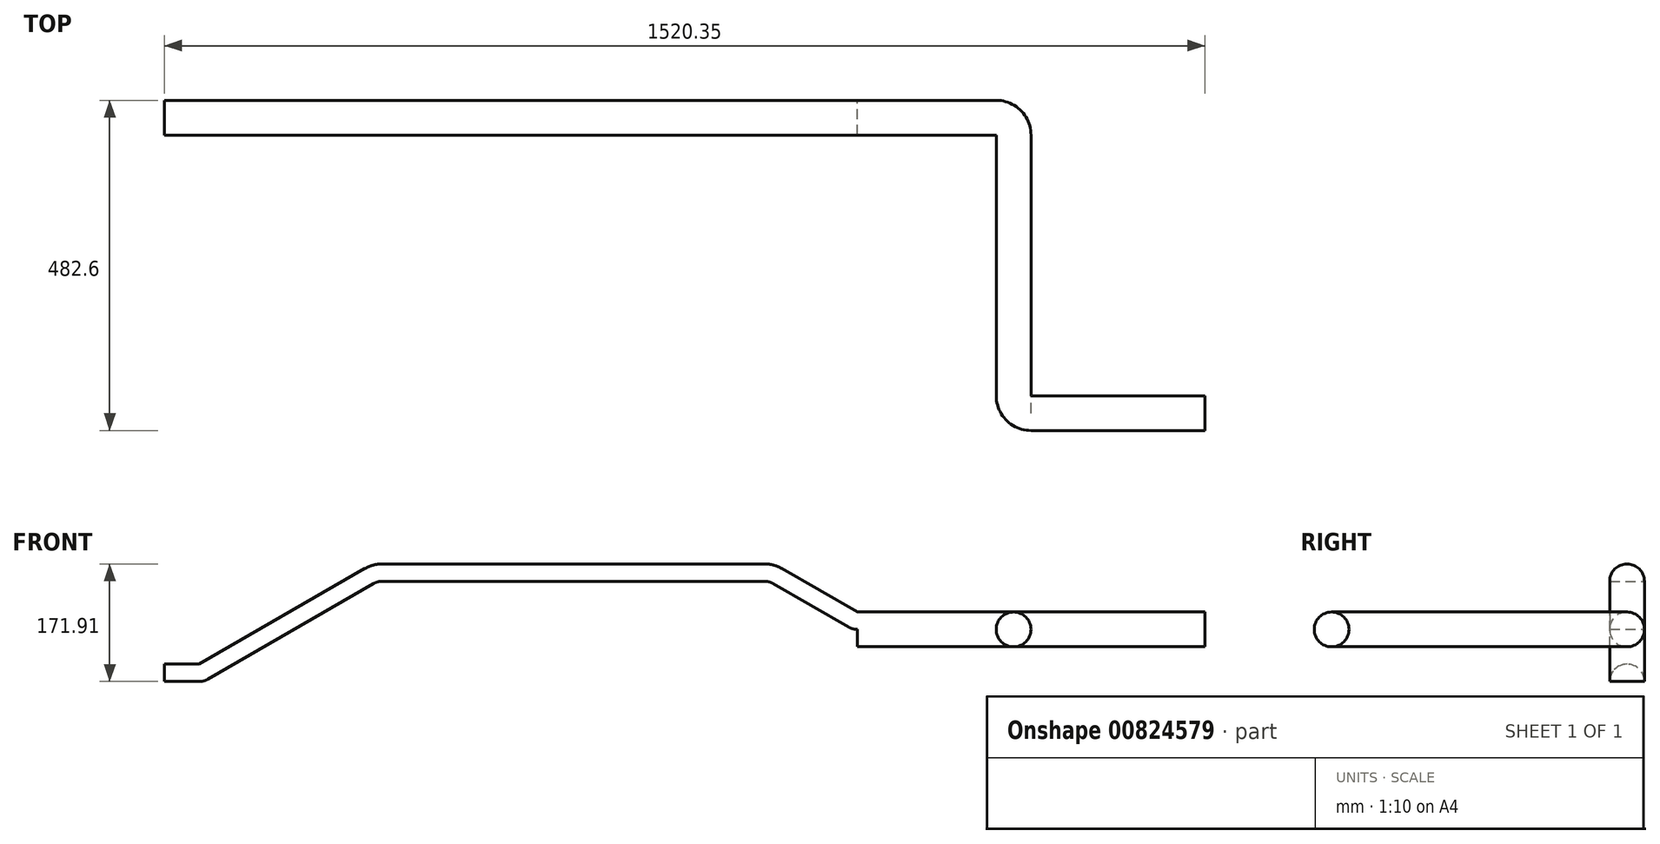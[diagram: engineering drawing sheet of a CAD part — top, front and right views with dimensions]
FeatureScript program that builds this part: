
annotation { "Feature Type Name" : "Feature", "Feature Type Description" : "" }
export const myFeature = defineFeature(function(context is Context, id is Id, definition is map)
    precondition{}
    {
        {
            var Q0;
            Q0=qCreatedBy(makeId("Right.planeOp"),FACE);
            var sketch = newSketch(context, id + "F0", { "sketchPlane" : qUnion([Q0])});
            skCircle(sketch, "E0", {"center": v(0, 0) * mm, "radius": 25.4 * mm});
            skSolve(sketch);
        }
        {
            var Q0;
            Q0=makeQuery(id+"F0.imprint","IMPRINT",FACE,{"disambiguationData":[TD([[makeQuery(id+"F0.imprint","IMPRINT",EDGE,{"derivedFrom":sQuery(id+"F0.wireOp",EDGE,"E0")}),1.0]])]});
            extrude(context, id + "F1", {"entities" : qUnion([Q0]), "oppositeDirection" : true, "depth" : 254 * mm, "offsetDistance" : 25.4 * mm});
        }
        {
            var Q0;
            Q0=makeQuery(id+"F1.opExtrude","CAP_FACE",FACE,{"disambiguationData":[OSD([sQuery(id+"F0.wireOp",EDGE,"E0")])],"isStart":false});
            var sketch = newSketch(context, id + "F2", { "sketchPlane" : qUnion([Q0])});
            skLineSegment(sketch, "E1", {"start": v(-25.4, 0) * mm, "end": v(-25.4, 47.8) * mm});
            skSolve(sketch);
        }
        {
            var Q0;
            Q0=makeQuery(id+"F2.imprint","IMPRINT",FACE,{"disambiguationData":[TD([[makeQuery(id+"F2.imprint","IMPRINT",EDGE,{"derivedFrom":makeQuery(id+"F1.opExtrude","CAP_EDGE",EDGE,{"disambiguationData":[OSD([sQuery(id+"F0.wireOp",EDGE,"E0")])],"isStart":false})}),-1.0]])]});
            var Q1;
            Q1=sQuery(id+"F2.wireOp",EDGE,"E1");
            revolve(context, id + "F3", {"operationType" : NewBodyOperationType.ADD, "surfaceOperationType" : NewSurfaceOperationType.NEW, "entities" : qUnion([Q0]), "axis" : qUnion([Q1]), "revolveType" : RevolveType.ONE_DIRECTION, "oppositeDirection" : true, "angle" : 90 * degree});
        }
        {
            var Q0;
            Q0=makeQuery(id+"F3.opRevolve","CAP_FACE",FACE,{"disambiguationData":[OSD([sQuery(id+"F0.wireOp",EDGE,"E0")])],"isStart":false});
            extrude(context, id + "F4", {"entities" : qUnion([Q0]), "operationType" : NewBodyOperationType.ADD, "depth" : 381 * mm, "offsetDistance" : 25.4 * mm});
        }
        {
            var Q0;
            Q0=makeQuery(id+"F4.opExtrude","CAP_FACE",FACE,{"disambiguationData":[OSD([sQuery(id+"F0.wireOp",EDGE,"E0")])],"isStart":false});
            var sketch = newSketch(context, id + "F5", { "sketchPlane" : qUnion([Q0])});
            skLineSegment(sketch, "E2", {"start": v(304.8, 0) * mm, "end": v(304.8, 42.25) * mm});
            skSolve(sketch);
        }
        {
            var Q0;
            Q0=makeQuery(id+"F5.imprint","IMPRINT",FACE,{"disambiguationData":[TD([[makeQuery(id+"F5.imprint","IMPRINT",EDGE,{"derivedFrom":makeQuery(id+"F4.opExtrude","CAP_EDGE",EDGE,{"disambiguationData":[OSD([sQuery(id+"F0.wireOp",EDGE,"E0")])],"isStart":false})}),-1.0]])]});
            var Q1;
            Q1=sQuery(id+"F5.wireOp",EDGE,"E2");
            revolve(context, id + "F6", {"operationType" : NewBodyOperationType.ADD, "surfaceOperationType" : NewSurfaceOperationType.NEW, "entities" : qUnion([Q0]), "axis" : qUnion([Q1]), "revolveType" : RevolveType.ONE_DIRECTION, "angle" : 90 * degree});
        }
        {
            var Q0;
            Q0=makeQuery(id+"F6.opRevolve","CAP_FACE",FACE,{"disambiguationData":[OSD([sQuery(id+"F0.wireOp",EDGE,"E0")])],"isStart":false});
            extrude(context, id + "F7", {"entities" : qUnion([Q0]), "operationType" : NewBodyOperationType.ADD, "depth" : 203.2 * mm, "offsetDistance" : 25.4 * mm});
        }
        {
            var Q0;
            Q0=makeQuery(id+"F7.opExtrude","CAP_FACE",FACE,{"disambiguationData":[OSD([sQuery(id+"F0.wireOp",EDGE,"E0")])],"isStart":false});
            var sketch = newSketch(context, id + "F8", { "sketchPlane" : qUnion([Q0])});
            skLineSegment(sketch, "E3", {"start": v(-406.4, 0) * mm, "end": v(-457.2, 0) * mm});
            skLineSegment(sketch, "E4", {"start": v(-431.8, 0) * mm, "end": v(-431.8, 25.4) * mm});
            skLineSegment(sketch, "E5", {"start": v(-431.8, 25.4) * mm, "end": v(-464.82, 25.4) * mm});
            skSolve(sketch);
        }
        {
            var Q0;
            {var subQ3=sQuery(id+"F8.wireOp",EDGE,"E4");Q0=makeQuery(id+"F8.imprint","IMPRINT",FACE,{"disambiguationData":[TD([[makeQuery(id+"F8.imprint","IMPRINT",EDGE,{"derivedFrom":subQ3}),-1.0]])]});}
            var Q1;
            {var subQ3=sQuery(id+"F8.wireOp",EDGE,"E4");Q1=makeQuery(id+"F8.imprint","IMPRINT",FACE,{"disambiguationData":[TD([[makeQuery(id+"F8.imprint","IMPRINT",EDGE,{"derivedFrom":subQ3}),1.0]])]});}
            var Q2;
            {var subQ0=sQuery(id+"F8.wireOp",EDGE,"E3");var subQ1=makeQuery(id+"F7.opExtrude","CAP_EDGE",EDGE,{"disambiguationData":[OSD([sQuery(id+"F0.wireOp",EDGE,"E0")])],"isStart":false});var subQ2=makeQuery(id+"F8.imprint","INTERSECT",VERTEX,{"disambiguationData":[OD(0.0)],"derivedFrom":[subQ1,subQ0]});Q2=makeQuery(id+"F8.imprint","IMPRINT",FACE,{"disambiguationData":[TD([[makeQuery(id+"F8.imprint","IMPRINT",EDGE,{"disambiguationData":[TD([[subQ2,-1.0]])],"derivedFrom":subQ0}),1.0]])]});}
            var Q3;
            Q3=sQuery(id+"F8.wireOp",EDGE,"E5");
            revolve(context, id + "F9", {"operationType" : NewBodyOperationType.ADD, "surfaceOperationType" : NewSurfaceOperationType.NEW, "entities" : qUnion([Q0, Q1, Q2]), "axis" : qUnion([Q3]), "revolveType" : RevolveType.ONE_DIRECTION, "angle" : 30 * degree});
        }
        {
            var Q0;
            Q0=makeQuery(id+"F9.opRevolve","CAP_FACE",FACE,{"disambiguationData":[OSD([sQuery(id+"F0.wireOp",EDGE,"E0")])],"isStart":false});
            extrude(context, id + "F10", {"entities" : qUnion([Q0]), "operationType" : NewBodyOperationType.ADD, "depth" : 127 * mm, "offsetDistance" : 25.4 * mm});
        }
        {
            var Q0;
            Q0=makeQuery(id+"F10.opExtrude","CAP_FACE",FACE,{"disambiguationData":[OSD([sQuery(id+"F0.wireOp",EDGE,"E0")])],"isStart":false});
            var sketch = newSketch(context, id + "F11", { "sketchPlane" : qUnion([Q0])});
            skLineSegment(sketch, "E6", {"start": v(-431.8, -257.4) * mm, "end": v(-431.8, -282.8) * mm});
            skLineSegment(sketch, "E7", {"start": v(-431.8, -282.8) * mm, "end": v(-393.58, -282.8) * mm});
            skSolve(sketch);
        }
        {
            var Q0;
            Q0=makeQuery(id+"F11.imprint","IMPRINT",FACE,{"disambiguationData":[TD([[makeQuery(id+"F11.imprint","IMPRINT",EDGE,{"derivedFrom":makeQuery(id+"F10.opExtrude","CAP_EDGE",EDGE,{"disambiguationData":[OSD([sQuery(id+"F0.wireOp",EDGE,"E0")])],"isStart":false})}),-1.0]])]});
            var Q1;
            Q1=sQuery(id+"F11.wireOp",EDGE,"E7");
            revolve(context, id + "F12", {"operationType" : NewBodyOperationType.ADD, "surfaceOperationType" : NewSurfaceOperationType.NEW, "entities" : qUnion([Q0]), "axis" : qUnion([Q1]), "revolveType" : RevolveType.ONE_DIRECTION, "angle" : 30 * degree});
        }
        {
            var Q0;
            Q0=makeQuery(id+"F12.opRevolve","CAP_FACE",FACE,{"disambiguationData":[OSD([sQuery(id+"F0.wireOp",EDGE,"E0")])],"isStart":false});
            extrude(context, id + "F13", {"entities" : qUnion([Q0]), "operationType" : NewBodyOperationType.ADD, "depth" : 558.8 * mm, "offsetDistance" : 25.4 * mm});
        }
        {
            var Q0;
            Q0=makeQuery(id+"F13.opExtrude","CAP_FACE",FACE,{"disambiguationData":[OSD([sQuery(id+"F0.wireOp",EDGE,"E0")])],"isStart":false});
            var sketch = newSketch(context, id + "F14", { "sketchPlane" : qUnion([Q0])});
            skLineSegment(sketch, "E8", {"start": v(-431.8, 70.3) * mm, "end": v(-431.8, 44.9) * mm});
            skLineSegment(sketch, "E9", {"start": v(-431.8, 44.9) * mm, "end": v(-398.81, 44.9) * mm});
            skSolve(sketch);
        }
        {
            var Q0;
            Q0=makeQuery(id+"F14.imprint","IMPRINT",FACE,{"disambiguationData":[TD([[makeQuery(id+"F14.imprint","IMPRINT",EDGE,{"derivedFrom":makeQuery(id+"F13.opExtrude","CAP_EDGE",EDGE,{"disambiguationData":[OSD([sQuery(id+"F0.wireOp",EDGE,"E0")])],"isStart":false})}),-1.0]])]});
            var Q1;
            Q1=sQuery(id+"F14.wireOp",EDGE,"E9");
            revolve(context, id + "F15", {"operationType" : NewBodyOperationType.ADD, "surfaceOperationType" : NewSurfaceOperationType.NEW, "entities" : qUnion([Q0]), "axis" : qUnion([Q1]), "revolveType" : RevolveType.ONE_DIRECTION, "angle" : 30 * degree});
        }
        {
            var Q0;
            Q0=makeQuery(id+"F15.opRevolve","CAP_FACE",FACE,{"disambiguationData":[OSD([sQuery(id+"F0.wireOp",EDGE,"E0")])],"isStart":false});
            extrude(context, id + "F16", {"entities" : qUnion([Q0]), "operationType" : NewBodyOperationType.ADD, "depth" : 279.4 * mm, "offsetDistance" : 25.4 * mm});
        }
        {
            var Q0;
            Q0=makeQuery(id+"F16.opExtrude","CAP_FACE",FACE,{"disambiguationData":[OSD([sQuery(id+"F0.wireOp",EDGE,"E0")])],"isStart":false});
            var sketch = newSketch(context, id + "F17", { "sketchPlane" : qUnion([Q0])});
            skLineSegment(sketch, "E10", {"start": v(-431.8, 665.38) * mm, "end": v(-431.8, 690.78) * mm});
            skLineSegment(sketch, "E11", {"start": v(-431.8, 690.78) * mm, "end": v(-475.64, 690.78) * mm});
            skSolve(sketch);
        }
        {
            var Q0;
            Q0=makeQuery(id+"F17.imprint","IMPRINT",FACE,{"disambiguationData":[TD([[makeQuery(id+"F17.imprint","IMPRINT",EDGE,{"derivedFrom":makeQuery(id+"F16.opExtrude","CAP_EDGE",EDGE,{"disambiguationData":[OSD([sQuery(id+"F0.wireOp",EDGE,"E0")])],"isStart":false})}),-1.0]])]});
            var Q1;
            Q1=sQuery(id+"F17.wireOp",EDGE,"E11");
            revolve(context, id + "F18", {"operationType" : NewBodyOperationType.ADD, "surfaceOperationType" : NewSurfaceOperationType.NEW, "entities" : qUnion([Q0]), "axis" : qUnion([Q1]), "revolveType" : RevolveType.ONE_DIRECTION, "angle" : 30 * degree});
        }
        {
            var Q0;
            Q0=makeQuery(id+"F18.opRevolve","CAP_FACE",FACE,{"disambiguationData":[OSD([sQuery(id+"F0.wireOp",EDGE,"E0")])],"isStart":false});
            extrude(context, id + "F19", {"entities" : qUnion([Q0]), "operationType" : NewBodyOperationType.ADD, "depth" : 50.8 * mm, "offsetDistance" : 25.4 * mm});
        }
    });
